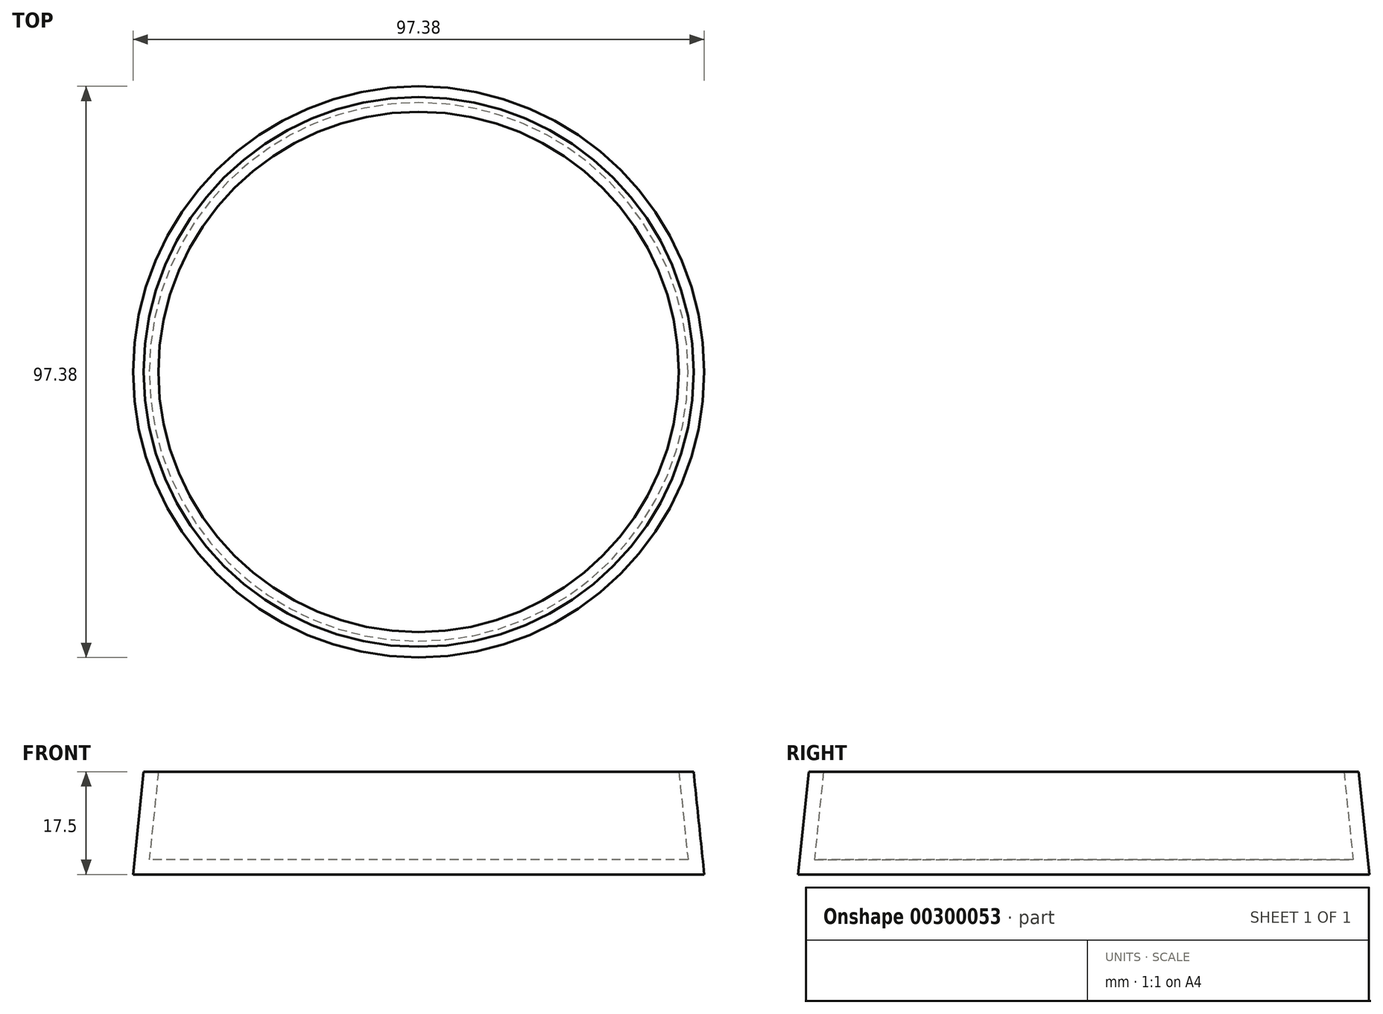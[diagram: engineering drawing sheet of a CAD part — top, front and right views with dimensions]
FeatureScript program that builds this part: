
annotation { "Feature Type Name" : "Feature", "Feature Type Description" : "" }
export const myFeature = defineFeature(function(context is Context, id is Id, definition is map)
    precondition{}
    {
        {
            assignVariable(context, id + "F0", {"name" : "bucket_t", "anyValue" : 0.75});
        }
        {
            assignVariable(context, id + "F1", {"name" : "bucket_top_d", "anyValue" : 117 - (getVariable(context, 'bucket_t') * 2)});
        }
        {
            assignVariable(context, id + "F2", {"name" : "bucket_bot_d", "anyValue" : 88 - (getVariable(context, 'bucket_t') * 2)});
        }
        {
            assignVariable(context, id + "F3", {"name" : "bucket_h", "anyValue" : 140});
        }
        {
            assignVariable(context, id + "F4", {"name" : "bucket_angle", "anyValue" : atan(((getVariable(context, 'bucket_top_d') - getVariable(context, 'bucket_bot_d')) / 2) / getVariable(context, 'bucket_h'))});
        }
        {
            assignVariable(context, id + "F5", {"name" : "screen_h", "anyValue" : 2.5});
        }
        {
            assignVariable(context, id + "F6", {"name" : "rim_h", "anyValue" : 15});
        }
        {
            assignVariable(context, id + "F7", {"name" : "spacer_h", "anyValue" : getVariable(context, 'screen_h') + getVariable(context, 'rim_h')});
        }
        {
            var Q0;
            Q0=qCreatedBy(makeId("Top.planeOp"),FACE);
            var sketch = newSketch(context, id + "F8", { "sketchPlane" : qUnion([Q0])});
            skCircle(sketch, "E0", {"center": v(0, 0) * mm, "radius": 48.69 * mm});
            skSolve(sketch);
        }
        {
            var Q0;
            Q0=makeQuery(id+"F8.imprint","IMPRINT",FACE,{"disambiguationData":[TD([[makeQuery(id+"F8.imprint","IMPRINT",EDGE,{"derivedFrom":sQuery(id+"F8.wireOp",EDGE,"E0")}),1.0]])]});
            extrude(context, id + "F9", {"entities" : qUnion([Q0]), "depth" : (getVariable(context, 'spacer_h')) * mm, "hasDraft" : true, "draftAngle" : getVariable(context, 'bucket_angle'), "draftPullDirection" : true});
        }
        {
            var Q0;
            Q0=makeQuery(id+"F9.opExtrude","CAP_FACE",FACE,{"disambiguationData":[OSD([sQuery(id+"F8.wireOp",EDGE,"E0")])],"isStart":false});
            shell(context, id + "F10", {"entities" : qUnion([Q0]), "thickness" : (getVariable(context, 'screen_h')) * mm});
        }
    });
